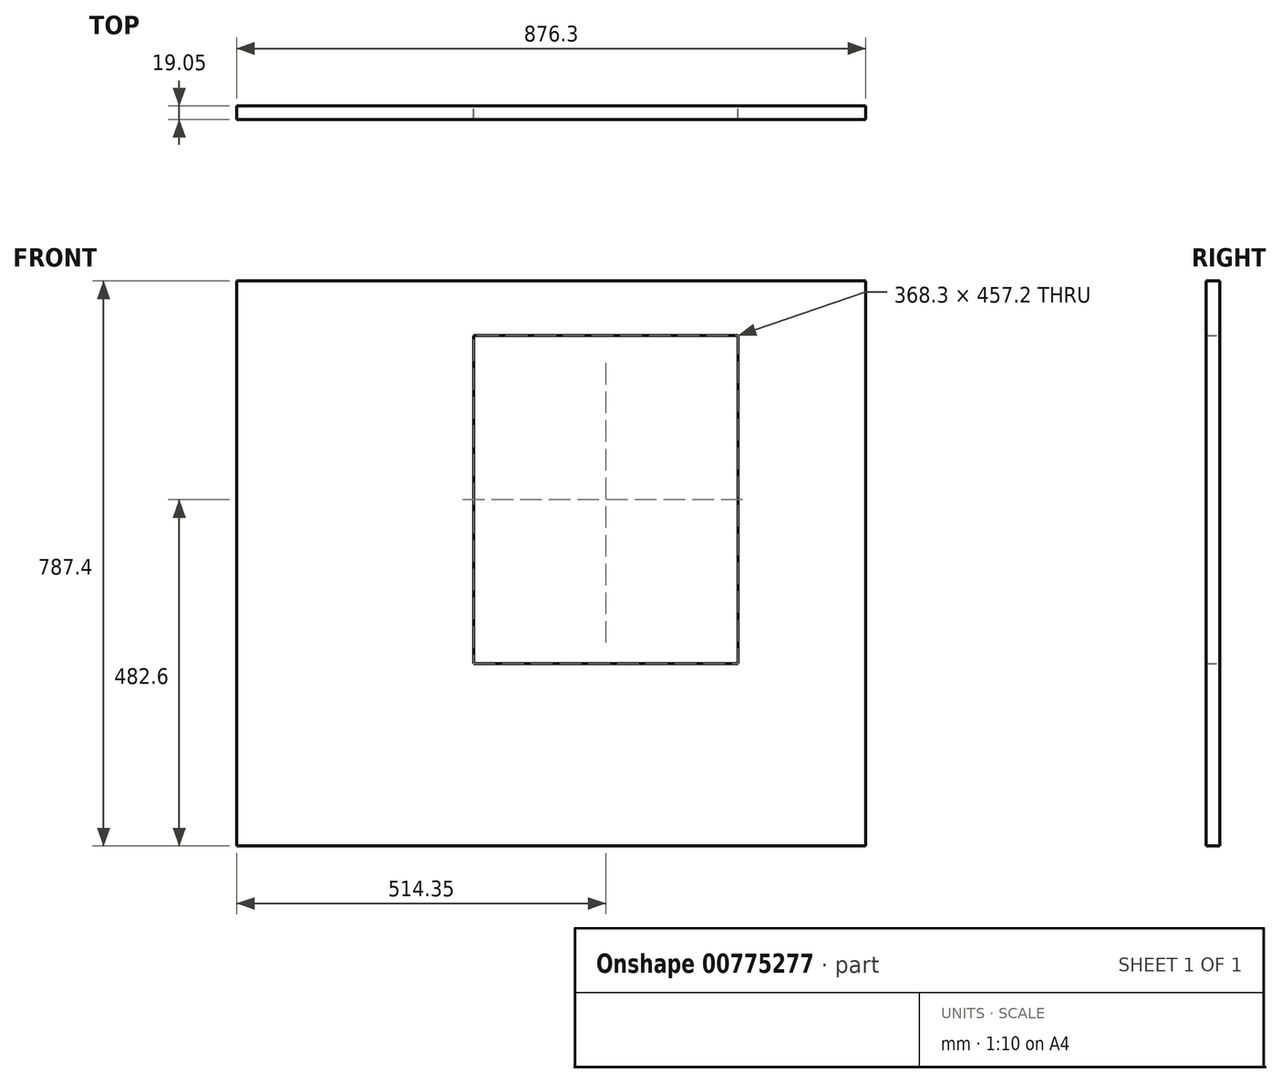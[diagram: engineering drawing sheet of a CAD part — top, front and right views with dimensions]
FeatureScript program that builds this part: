
annotation { "Feature Type Name" : "Feature", "Feature Type Description" : "" }
export const myFeature = defineFeature(function(context is Context, id is Id, definition is map)
    precondition{}
    {
        {
            var Q0;
            Q0=qCreatedBy(makeId("Front.planeOp"),FACE);
            var sketch = newSketch(context, id + "F0", { "sketchPlane" : qUnion([Q0])});
            skLineSegment(sketch, "E0.bottom", {"start": v(0, 0) * mm, "end": v(-876.3, 0) * mm});
            skLineSegment(sketch, "E0.top", {"start": v(0, 787.4) * mm, "end": v(-876.3, 787.4) * mm});
            skLineSegment(sketch, "E0.left", {"start": v(0, 0) * mm, "end": v(0, 787.4) * mm});
            skLineSegment(sketch, "E0.right", {"start": v(-876.3, 0) * mm, "end": v(-876.3, 787.4) * mm});
            skLineSegment(sketch, "E1.bottom", {"start": v(-546.1, 711.2) * mm, "end": v(-177.8, 711.2) * mm});
            skLineSegment(sketch, "E1.top", {"start": v(-546.1, 254) * mm, "end": v(-177.8, 254) * mm});
            skLineSegment(sketch, "E1.left", {"start": v(-546.1, 711.2) * mm, "end": v(-546.1, 254) * mm});
            skLineSegment(sketch, "E1.right", {"start": v(-177.8, 711.2) * mm, "end": v(-177.8, 254) * mm});
            skSolve(sketch);
        }
        {
            var Q0;
            Q0 = qSketchRegion(id + "F0", true);
            extrude(context, id + "F1", {"entities" : qUnion([Q0]), "depth" : 19.05 * mm, "offsetDistance" : 25.4 * mm});
        }
    });
